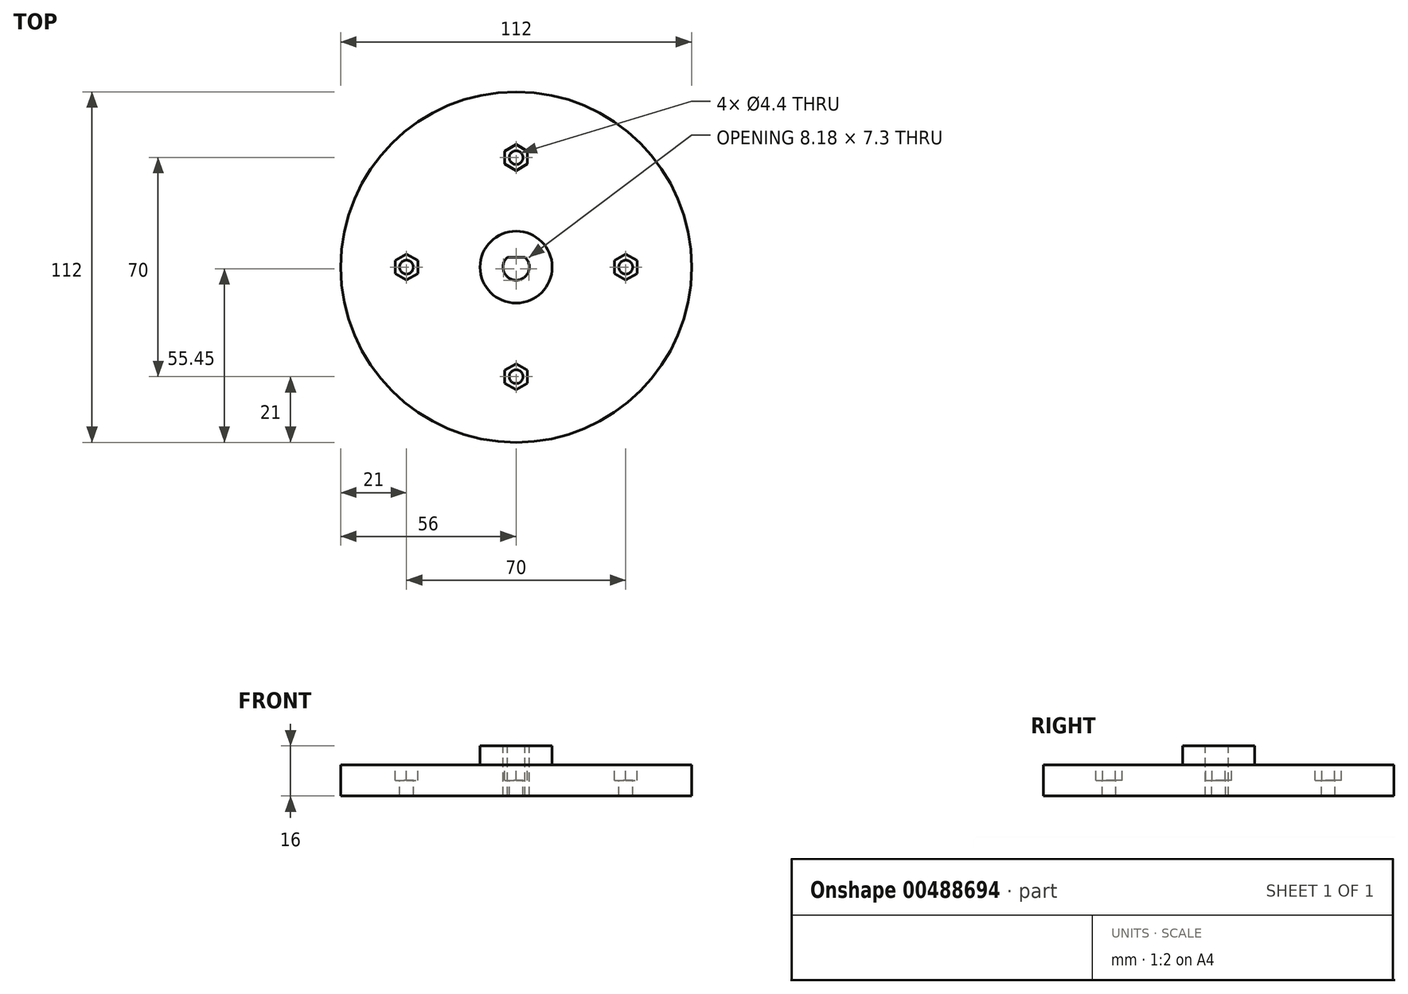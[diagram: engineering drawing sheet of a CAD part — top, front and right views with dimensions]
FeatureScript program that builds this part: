
annotation { "Feature Type Name" : "Feature", "Feature Type Description" : "" }
export const myFeature = defineFeature(function(context is Context, id is Id, definition is map)
    precondition{}
    {
        {
            var Q0;
            Q0=qCreatedBy(makeId("Top.planeOp"),FACE);
            var sketch = newSketch(context, id + "F0", { "sketchPlane" : qUnion([Q0])});
            skCircle(sketch, "E0", {"center": v(0, 0) * mm, "radius": 56 * mm});
            skSolve(sketch);
        }
        {
            var Q0;
            Q0 = qSketchRegion(id + "F0", true);
            extrude(context, id + "F1", {"entities" : qUnion([Q0]), "depth" : 10 * mm});
        }
        {
            var Q0;
            Q0=makeQuery(id+"F1.opExtrude","CAP_FACE",FACE,{"disambiguationData":[OSD([sQuery(id+"F0.wireOp",EDGE,"E0")])],"isStart":false});
            var sketch = newSketch(context, id + "F2", { "sketchPlane" : qUnion([Q0])});
            skCircle(sketch, "E1", {"center": v(0, 0) * mm, "radius": 11.5 * mm});
            skSolve(sketch);
        }
        {
            var Q0;
            Q0 = qSketchRegion(id + "F2", true);
            extrude(context, id + "F3", {"entities" : qUnion([Q0]), "operationType" : NewBodyOperationType.ADD, "depth" : 6 * mm});
        }
        {
            var Q0;
            Q0=makeQuery(id+"F3.opExtrude","CAP_FACE",FACE,{"disambiguationData":[OSD([sQuery(id+"F2.wireOp",EDGE,"E1")])],"isStart":false});
            var sketch = newSketch(context, id + "F4", { "sketchPlane" : qUnion([Q0])});
            skArc(sketch, "E2", {"start": v(-2.83, 3.1) * mm, "mid": v(0, -4.2) * mm, "end": v(2.83, 3.1) * mm});
            skLineSegment(sketch, "E3", {"start": v(-2.83, 3.1) * mm, "end": v(2.83, 3.1) * mm});
            skSolve(sketch);
        }
        {
            var Q0;
            Q0 = qSketchRegion(id + "F4", true);
            extrude(context, id + "F5", {"entities" : qUnion([Q0]), "operationType" : NewBodyOperationType.REMOVE, "oppositeDirection" : true, "depth" : 16 * mm});
        }
        {
            var Q0;
            Q0=makeQuery(id+"F1.opExtrude","CAP_FACE",FACE,{"disambiguationData":[OSD([sQuery(id+"F0.wireOp",EDGE,"E0")])],"isStart":false});
            var sketch = newSketch(context, id + "F6", { "sketchPlane" : qUnion([Q0])});
            skCircle(sketch, "E4", {"center": v(0, 0) * mm, "radius": 35 * mm, "construction": true});
            skCircle(sketch, "E5", {"center": v(0, 35) * mm, "radius": 2.2 * mm});
            skCircle(sketch, "E6", {"center": v(35, 0) * mm, "radius": 2.2 * mm});
            skCircle(sketch, "E7", {"center": v(-35, 0) * mm, "radius": 2.2 * mm});
            skCircle(sketch, "E8", {"center": v(0, -35) * mm, "radius": 2.2 * mm});
            skSolve(sketch);
        }
        {
            var Q0;
            Q0 = qSketchRegion(id + "F6", true);
            extrude(context, id + "F7", {"entities" : qUnion([Q0]), "operationType" : NewBodyOperationType.REMOVE, "oppositeDirection" : true, "depth" : 10 * mm});
        }
        {
            var Q0;
            Q0=makeQuery(id+"F1.opExtrude","CAP_FACE",FACE,{"disambiguationData":[OSD([sQuery(id+"F0.wireOp",EDGE,"E0")])],"isStart":false});
            var sketch = newSketch(context, id + "F8", { "sketchPlane" : qUnion([Q0])});
            skCircle(sketch, "E9.cCircle", {"center": v(0, 35) * mm, "radius": 3.6 * mm, "construction": true});
            skLineSegment(sketch, "E9.0", {"start": v(3.6, 37.08) * mm, "end": v(3.6, 32.92) * mm});
            skLineSegment(sketch, "E9.1", {"start": v(3.6, 32.92) * mm, "end": v(0, 30.84) * mm});
            skLineSegment(sketch, "E9.2", {"start": v(0, 30.84) * mm, "end": v(-3.6, 32.92) * mm});
            skLineSegment(sketch, "E9.3", {"start": v(-3.6, 32.92) * mm, "end": v(-3.6, 37.08) * mm});
            skLineSegment(sketch, "E9.4", {"start": v(-3.6, 37.08) * mm, "end": v(0, 39.16) * mm});
            skLineSegment(sketch, "E9.5", {"start": v(0, 39.16) * mm, "end": v(3.6, 37.08) * mm});
            skPoint(sketch, "E9.0.midPoint", {"position": v(3.6, 35) * mm});
            skCircle(sketch, "E10.cCircle", {"center": v(35, 0) * mm, "radius": 3.6 * mm, "construction": true});
            skLineSegment(sketch, "E10.0", {"start": v(38.6, 2.08) * mm, "end": v(38.6, -2.08) * mm});
            skLineSegment(sketch, "E10.1", {"start": v(38.6, -2.08) * mm, "end": v(35, -4.16) * mm});
            skLineSegment(sketch, "E10.2", {"start": v(35, -4.16) * mm, "end": v(31.4, -2.08) * mm});
            skLineSegment(sketch, "E10.3", {"start": v(31.4, -2.08) * mm, "end": v(31.4, 2.08) * mm});
            skLineSegment(sketch, "E10.4", {"start": v(31.4, 2.08) * mm, "end": v(35, 4.16) * mm});
            skLineSegment(sketch, "E10.5", {"start": v(35, 4.16) * mm, "end": v(38.6, 2.08) * mm});
            skPoint(sketch, "E10.0.midPoint", {"position": v(38.6, 0) * mm});
            skCircle(sketch, "E11.cCircle", {"center": v(0, -35) * mm, "radius": 3.6 * mm, "construction": true});
            skLineSegment(sketch, "E11.0", {"start": v(3.6, -32.92) * mm, "end": v(3.6, -37.08) * mm});
            skLineSegment(sketch, "E11.1", {"start": v(3.6, -37.08) * mm, "end": v(0, -39.16) * mm});
            skLineSegment(sketch, "E11.2", {"start": v(0, -39.16) * mm, "end": v(-3.6, -37.08) * mm});
            skLineSegment(sketch, "E11.3", {"start": v(-3.6, -37.08) * mm, "end": v(-3.6, -32.92) * mm});
            skLineSegment(sketch, "E11.4", {"start": v(-3.6, -32.92) * mm, "end": v(0, -30.84) * mm});
            skLineSegment(sketch, "E11.5", {"start": v(0, -30.84) * mm, "end": v(3.6, -32.92) * mm});
            skPoint(sketch, "E11.0.midPoint", {"position": v(3.6, -35) * mm});
            skCircle(sketch, "E12.cCircle", {"center": v(-35, 0) * mm, "radius": 3.6 * mm, "construction": true});
            skLineSegment(sketch, "E12.0", {"start": v(-31.4, 2.08) * mm, "end": v(-31.4, -2.08) * mm});
            skLineSegment(sketch, "E12.1", {"start": v(-31.4, -2.08) * mm, "end": v(-35, -4.16) * mm});
            skLineSegment(sketch, "E12.2", {"start": v(-35, -4.16) * mm, "end": v(-38.6, -2.08) * mm});
            skLineSegment(sketch, "E12.3", {"start": v(-38.6, -2.08) * mm, "end": v(-38.6, 2.08) * mm});
            skLineSegment(sketch, "E12.4", {"start": v(-38.6, 2.08) * mm, "end": v(-35, 4.16) * mm});
            skLineSegment(sketch, "E12.5", {"start": v(-35, 4.16) * mm, "end": v(-31.4, 2.08) * mm});
            skPoint(sketch, "E12.0.midPoint", {"position": v(-31.4, 0) * mm});
            skSolve(sketch);
        }
        {
            var Q0;
            Q0 = qSketchRegion(id + "F8", true);
            extrude(context, id + "F9", {"entities" : qUnion([Q0]), "operationType" : NewBodyOperationType.REMOVE, "oppositeDirection" : true, "depth" : 5 * mm});
        }
    });
